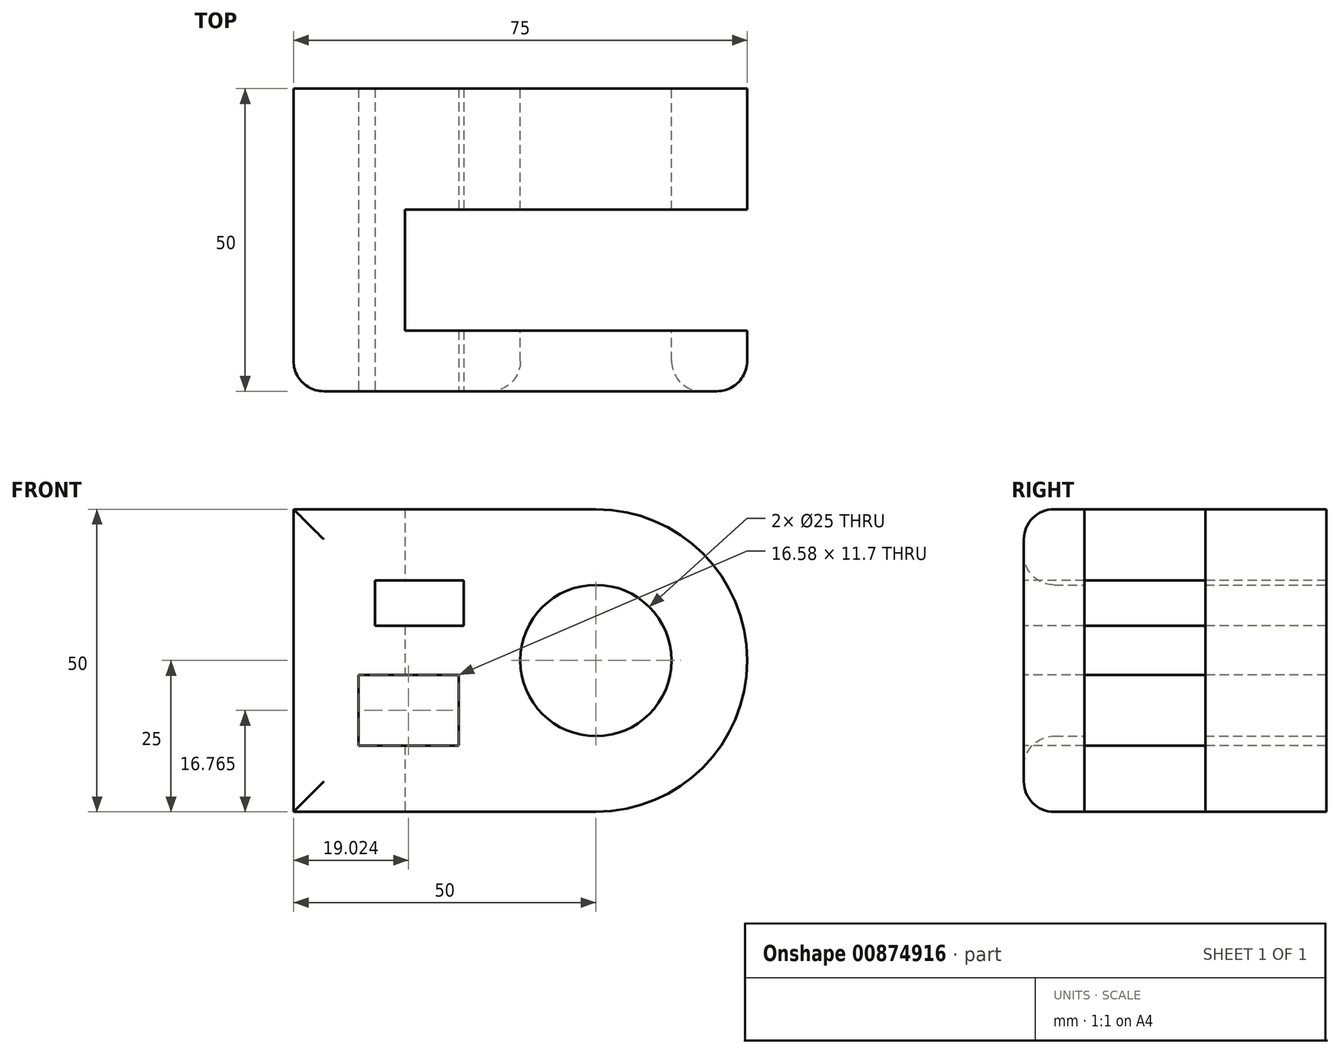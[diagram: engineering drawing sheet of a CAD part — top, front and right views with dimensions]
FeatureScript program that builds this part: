
annotation { "Feature Type Name" : "Feature", "Feature Type Description" : "" }
export const myFeature = defineFeature(function(context is Context, id is Id, definition is map)
    precondition{}
    {
        {
            var Q0;
            Q0=qCreatedBy(makeId("Front.planeOp"),FACE);
            var sketch = newSketch(context, id + "F0", { "sketchPlane" : qUnion([Q0])});
            skCircle(sketch, "E0", {"center": v(0, 0) * mm, "radius": 12.5 * mm});
            skArc(sketch, "E1", {"start": v(0, -25) * mm, "mid": v(25, 0) * mm, "end": v(0, 25) * mm});
            skLineSegment(sketch, "E2", {"start": v(0, 33.54) * mm, "end": v(0, -25) * mm, "construction": true});
            skLineSegment(sketch, "E3", {"start": v(0, 25) * mm, "end": v(-50, 25) * mm});
            skLineSegment(sketch, "E4", {"start": v(-50, 25) * mm, "end": v(-50, -25) * mm});
            skLineSegment(sketch, "E5", {"start": v(0, -25) * mm, "end": v(-50, -25) * mm});
            skSolve(sketch);
        }
        {
            var Q0;
            Q0 = qSketchRegion(id + "F0", true);
            extrude(context, id + "F1", {"entities" : qUnion([Q0]), "depth" : 20 * mm, "offsetDistance" : 25 * mm});
        }
        {
            var Q0;
            Q0=makeQuery(id+"F1.opExtrude","CAP_FACE",FACE,{"disambiguationData":[OSD([sQuery(id+"F0.wireOp",EDGE,"E0"),sQuery(id+"F0.wireOp",EDGE,"E1"),sQuery(id+"F0.wireOp",EDGE,"E3"),sQuery(id+"F0.wireOp",EDGE,"E4"),sQuery(id+"F0.wireOp",EDGE,"E5")])],"isStart":false});
            cPlane(context, id + "F2", {"entities" : qUnion([Q0]), "cplaneType" : CPlaneType.OFFSET, "offset" : 20 * mm, "width" : 150 * mm, "height" : 150 * mm});
        }
        {
            var Q0;
            Q0=qCreatedBy(id+"F2.planeOp",FACE);
            var sketch = newSketch(context, id + "F3", { "sketchPlane" : qUnion([Q0])});
            skLineSegment(sketch, "E6.0.0", {"start": v(-50, -25) * mm, "end": v(0, -25) * mm});
            skArc(sketch, "E6.0.1", {"start": v(0, -25) * mm, "mid": v(25, 0) * mm, "end": v(0, 25) * mm});
            skLineSegment(sketch, "E6.0.2", {"start": v(0, 25) * mm, "end": v(-50, 25) * mm});
            skLineSegment(sketch, "E6.0.3", {"start": v(-50, 25) * mm, "end": v(-50, -25) * mm});
            skCircle(sketch, "E7.0", {"center": v(0, 0) * mm, "radius": 12.5 * mm});
            skSolve(sketch);
        }
        {
            var Q0;
            Q0 = qSketchRegion(id + "F3", true);
            extrude(context, id + "F4", {"entities" : qUnion([Q0]), "depth" : 10 * mm, "offsetDistance" : 25 * mm});
        }
        {
            var Q0;
            Q0=makeQuery(id+"F1.opExtrude","CAP_FACE",FACE,{"disambiguationData":[OSD([sQuery(id+"F0.wireOp",EDGE,"E0"),sQuery(id+"F0.wireOp",EDGE,"E1"),sQuery(id+"F0.wireOp",EDGE,"E3"),sQuery(id+"F0.wireOp",EDGE,"E4"),sQuery(id+"F0.wireOp",EDGE,"E5")])],"isStart":false});
            var sketch = newSketch(context, id + "F5", { "sketchPlane" : qUnion([Q0])});
            skLineSegment(sketch, "E8.bottom", {"start": v(-50, 25) * mm, "end": v(-31.55, 25) * mm});
            skLineSegment(sketch, "E8.top", {"start": v(-50, -25) * mm, "end": v(-31.55, -25) * mm});
            skLineSegment(sketch, "E8.left", {"start": v(-50, 25) * mm, "end": v(-50, -25) * mm});
            skLineSegment(sketch, "E8.right", {"start": v(-31.55, 25) * mm, "end": v(-31.55, -25) * mm});
            skSolve(sketch);
        }
        {
            var Q0;
            Q0 = qSketchRegion(id + "F5", true);
            var Q1;
            Q1=makeQuery(id+"F4.opExtrude","CAP_FACE",FACE,{"disambiguationData":[OSD([sQuery(id+"F3.wireOp",EDGE,"E6.0.0"),sQuery(id+"F3.wireOp",EDGE,"E6.0.1"),sQuery(id+"F3.wireOp",EDGE,"E6.0.2"),sQuery(id+"F3.wireOp",EDGE,"E6.0.3"),sQuery(id+"F3.wireOp",EDGE,"E7.0")])],"isStart":true});
            extrude(context, id + "F6", {"entities" : qUnion([Q0]), "operationType" : NewBodyOperationType.ADD, "endBound" : BoundingType.UP_TO_SURFACE, "depth" : 25 * mm, "endBoundEntityFace" : qUnion([Q1]), "offsetDistance" : 25 * mm});
        }
        {
            var Q0;
            Q0=makeQuery(id+"F4.opExtrude","CAP_FACE",FACE,{"disambiguationData":[OSD([sQuery(id+"F3.wireOp",EDGE,"E6.0.0"),sQuery(id+"F3.wireOp",EDGE,"E6.0.1"),sQuery(id+"F3.wireOp",EDGE,"E6.0.2"),sQuery(id+"F3.wireOp",EDGE,"E6.0.3"),sQuery(id+"F3.wireOp",EDGE,"E7.0")])],"isStart":false});
            fillet(context, id + "F7", {"entities" : qUnion([Q0]), "radius" : 5 * mm, "tangentPropagation" : true, "allowEdgeOverflow" : false});
        }
        {
            var Q0;
            Q0=makeQuery(id+"F4.opExtrude","CAP_FACE",FACE,{"disambiguationData":[OSD([sQuery(id+"F3.wireOp",EDGE,"E6.0.0"),sQuery(id+"F3.wireOp",EDGE,"E6.0.1"),sQuery(id+"F3.wireOp",EDGE,"E6.0.2"),sQuery(id+"F3.wireOp",EDGE,"E6.0.3"),sQuery(id+"F3.wireOp",EDGE,"E7.0")])],"isStart":false});
            var sketch = newSketch(context, id + "F8", { "sketchPlane" : qUnion([Q0])});
            skLineSegment(sketch, "E9.bottom", {"start": v(-36.5, 13.22) * mm, "end": v(-21.88, 13.22) * mm});
            skLineSegment(sketch, "E9.top", {"start": v(-36.5, 5.74) * mm, "end": v(-21.88, 5.74) * mm});
            skLineSegment(sketch, "E9.left", {"start": v(-36.5, 13.22) * mm, "end": v(-36.5, 5.74) * mm});
            skLineSegment(sketch, "E9.right", {"start": v(-21.88, 13.22) * mm, "end": v(-21.88, 5.74) * mm});
            skLineSegment(sketch, "E10.bottom", {"start": v(-22.69, -2.38) * mm, "end": v(-39.26, -2.38) * mm});
            skLineSegment(sketch, "E10.top", {"start": v(-22.69, -14.08) * mm, "end": v(-39.26, -14.08) * mm});
            skLineSegment(sketch, "E10.left", {"start": v(-22.69, -2.38) * mm, "end": v(-22.69, -14.08) * mm});
            skLineSegment(sketch, "E10.right", {"start": v(-39.26, -2.38) * mm, "end": v(-39.26, -14.08) * mm});
            skPoint(sketch, "E10.middle", {"position": v(-30.98, -8.23) * mm});
            skSolve(sketch);
        }
        {
            var Q0;
            Q0 = qSketchRegion(id + "F8", true);
            extrude(context, id + "F9", {"entities" : qUnion([Q0]), "operationType" : NewBodyOperationType.REMOVE, "endBound" : BoundingType.THROUGH_ALL, "oppositeDirection" : true, "depth" : 25 * mm, "offsetDistance" : 25 * mm});
        }
    });
